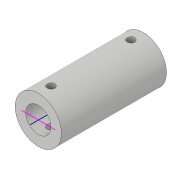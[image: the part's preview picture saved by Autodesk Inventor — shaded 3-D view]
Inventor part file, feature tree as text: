
AUTODESK INVENTOR PART (.ipt)
format: ipt  version: 2019 (Build 230136000, 136)  size: 117,248 bytes
history: native  units: in
note: dims shown in document units (in); Inventor stores cm internally (conversion verified against a paired STEP export)
features: sketch x5, extrude x3
ambient origin geometry x8: Origin, YZ Plane, XZ Plane, XY Plane, X Axis, Y Axis, Z Axis, Center Point
bodies: Solid1 (feature_tree)
feature tree (8):
  extrude  "Extrusion1"  Depth=0.2362in
  extrude  "Extrusion2"  Depth=0.0787in
  sketch  "Sketch3"  dims[d7=0.0394in d8=0.0709in]
  sketch  "Sketch4"  dims[d9=0.1181in]
  extrude  "Extrusion3"  Depth=0.0709in
  sketch  "Sketch1"  dims[d1=0.9843in d2=0.0in d3=0.2362in]
  sketch  "Sketch2"  dims[d4=0.0in d5=0.0in d6=0.0787in]
  sketch  "Sketch5"  dims[d10=0.0709in d11=0.0in d12=0.0in d13=0.4331in]
